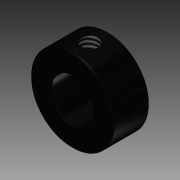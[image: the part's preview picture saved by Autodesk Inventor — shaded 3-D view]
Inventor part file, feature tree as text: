
AUTODESK INVENTOR PART (.ipt)
format: ipt  version: 2014 (Build 180170000, 170)  size: 117,248 bytes
history: native  units: in
note: dims shown in document units (in); Inventor stores cm internally (conversion verified against a paired STEP export)
features: sketch x3, extrude x2, chamfer x1, plane x1, hole x1
ambient origin geometry x8: Origin, YZ Plane, XZ Plane, XY Plane, X Axis, Y Axis, Z Axis, Center Point
bodies: Solid1 (feature_tree)
feature tree (8):
  extrude  "Extrusion1"  Depth=0.438in TaperAngle=0.0deg
  extrude  "Extrusion2"  Depth=0.5in TaperAngle=0.0deg
  chamfer  "Chamfer1"  Distance=0.0156in Angle=45.0deg
  plane  "Work Plane1"
  hole  "Hole1"  [1 undecoded]
  sketch  "Sketch1"  dims[d0=1.0in d1=0.438in d2=0.0in]
  sketch  "Sketch2"  dims[d3=0.5in d4=0.281in d5=0.0in d6=0.0156in d7=0.125in d8=45.0deg]
  sketch  "Sketch3"  dims[d9=0.196in d10=0.75in d11=0.375in d12=0.25in d13=0.5635in d14=1.0in d15=0.8108in]
note: 1 required parameter value undecoded (feature->parameter linkage not recoverable at this tier; creation-order binding heuristic only, values carry confidence <= 0.55)
